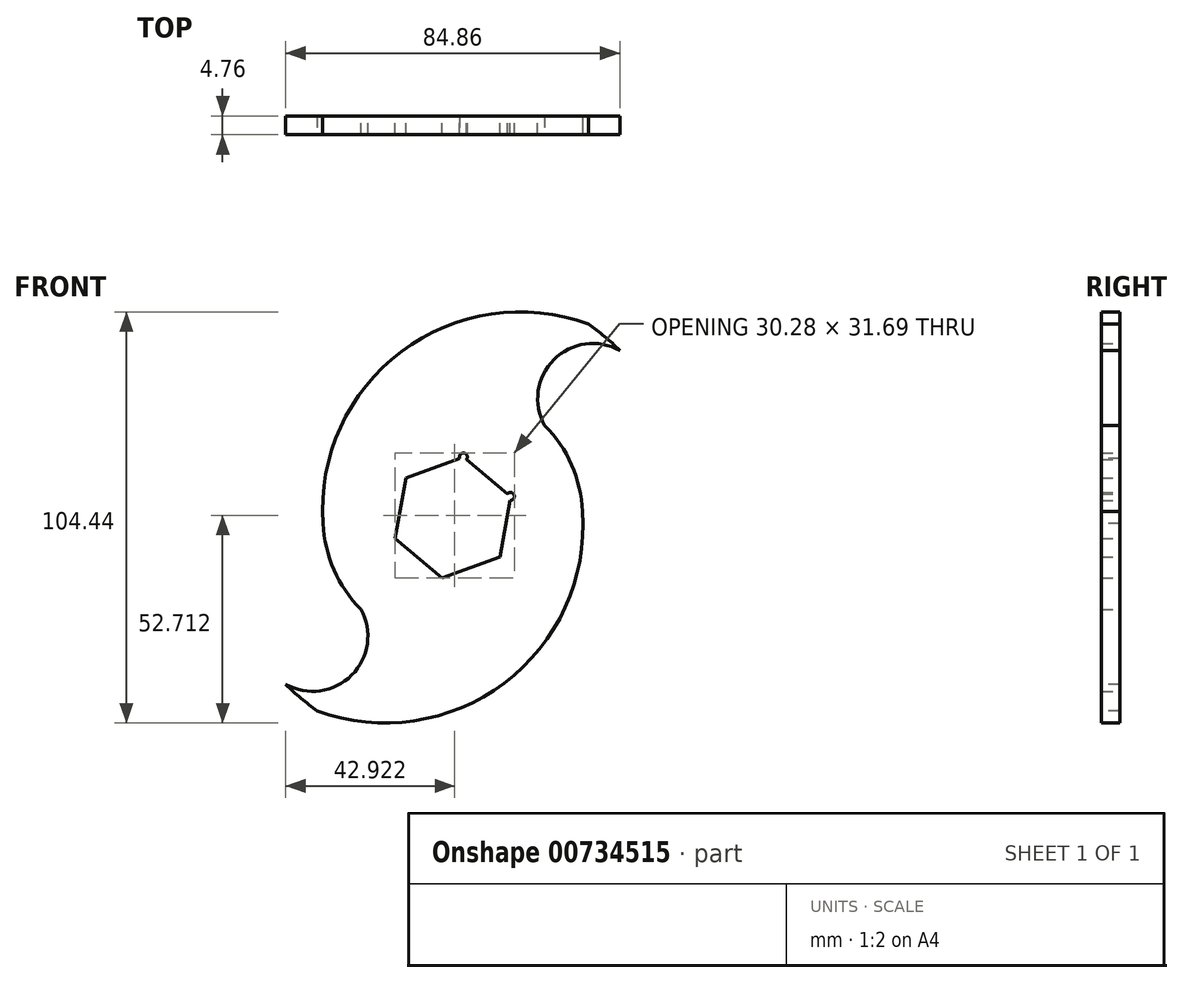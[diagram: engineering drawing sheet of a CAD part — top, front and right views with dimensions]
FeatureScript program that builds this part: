
annotation { "Feature Type Name" : "Feature", "Feature Type Description" : "" }
export const myFeature = defineFeature(function(context is Context, id is Id, definition is map)
    precondition{}
    {
        {
            var Q0;
            Q0=qCreatedBy(makeId("Front.planeOp"),FACE);
            var sketch = newSketch(context, id + "F0", { "sketchPlane" : qUnion([Q0])});
            skArc(sketch, "E0", {"start": v(13.88, 5.97) * mm, "mid": v(15.59, 5.67) * mm, "end": v(14.47, 4.35) * mm});
            skLineSegment(sketch, "E1", {"start": v(14.47, 4.35) * mm, "end": v(11.94, -10.02) * mm});
            skLineSegment(sketch, "E2", {"start": v(11.94, -10.02) * mm, "end": v(-2.7, -15.35) * mm});
            skLineSegment(sketch, "E3", {"start": v(-2.7, -15.35) * mm, "end": v(-14.65, -5.33) * mm});
            skLineSegment(sketch, "E4", {"start": v(-14.65, -5.33) * mm, "end": v(-11.94, 10.02) * mm});
            skLineSegment(sketch, "E5", {"start": v(-11.94, 10.02) * mm, "end": v(1.77, 15) * mm});
            skArc(sketch, "E6", {"start": v(1.77, 15) * mm, "mid": v(2.88, 16.34) * mm, "end": v(3.47, 14.7) * mm});
            skLineSegment(sketch, "E7", {"start": v(3.47, 14.7) * mm, "end": v(13.88, 5.97) * mm});
            skArc(sketch, "E8", {"start": v(-23.33, -23.33) * mm, "mid": v(-25.68, -40.08) * mm, "end": v(-42.43, -42.43) * mm});
            skArc(sketch, "E9", {"start": v(-42.43, -42.43) * mm, "mid": v(-38.57, -45.96) * mm, "end": v(-34.43, -49.14) * mm});
            skArc(sketch, "E10", {"start": v(-34.43, -49.14) * mm, "mid": v(13.05, -42.14) * mm, "end": v(32.97, 1.52) * mm});
            skArc(sketch, "E11", {"start": v(32.97, 1.52) * mm, "mid": v(30.19, 13.33) * mm, "end": v(23.33, 23.33) * mm});
            skArc(sketch, "E12", {"start": v(23.33, 23.33) * mm, "mid": v(25.68, 40.08) * mm, "end": v(42.43, 42.43) * mm});
            skArc(sketch, "E13", {"start": v(42.43, 42.43) * mm, "mid": v(38.57, 45.96) * mm, "end": v(34.43, 49.14) * mm});
            skArc(sketch, "E14", {"start": v(34.43, 49.14) * mm, "mid": v(-13.05, 42.14) * mm, "end": v(-32.97, -1.52) * mm});
            skArc(sketch, "E15", {"start": v(-32.97, -1.52) * mm, "mid": v(-30.19, -13.33) * mm, "end": v(-23.33, -23.33) * mm});
            skSolve(sketch);
        }
        {
            var Q0;
            Q0 = qSketchRegion(id + "F0", true);
            extrude(context, id + "F1", {"entities" : qUnion([Q0]), "depth" : 4.76 * mm, "offsetDistance" : 25.4 * mm});
        }
    });
